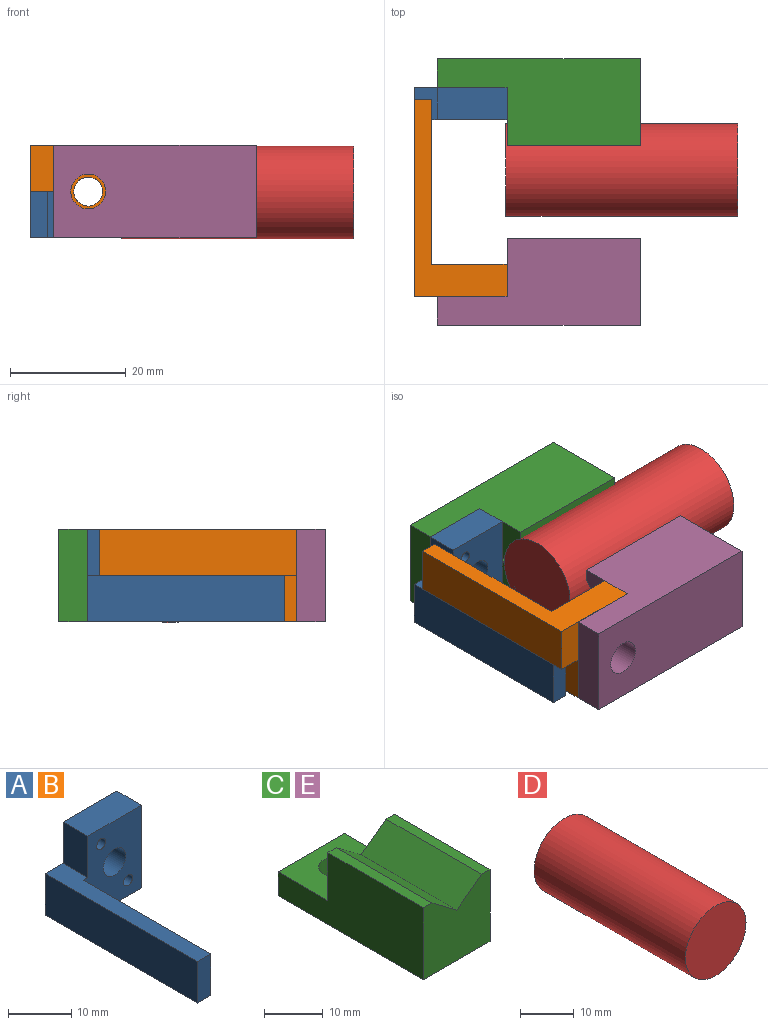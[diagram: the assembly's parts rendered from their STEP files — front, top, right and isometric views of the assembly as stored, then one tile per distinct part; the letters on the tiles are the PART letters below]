
ASSEMBLY  parts=5 mates=4
PART A: 13 faces, bbox 16x34x16 mm
  f0: plane 12x5.5mm, normal (0,0,1), area 66mm2, adj f3,f4,f5,f7
  f1: plane 34x8mm, normal (-1,0,0), area 272mm2, adj f2,f5,f6,f12
  f2: plane 34x16mm, normal (0,0,-1), area 173.5mm2, adj f1,f3,f4,f5,f11,f12
  f3: plane 16x5.5mm, normal (1,0,0), area 88mm2, adj f0,f2,f4,f5
  f4: plane 16x13mm, normal (0,-1,0), area 174.1mm2, adj f0,f2,f3,f6,f7,f8,f9,f10
  f5: plane 16x16mm, normal (0,1,0), area 198.1mm2, adj f0,f1,f2,f3,f6,f7,f8,f9
  f6: plane 34x4mm, normal (0,0,1), area 107.5mm2, adj f1,f4,f5,f7,f11,f12
  f7: plane 8x5.5mm, normal (-1,0,0), area 44mm2, adj f0,f4,f5,f6
  f8: cylinder r=1mm len=5.5mm, axis (0,-1,0), area 34.6mm2, adj f4,f5
  f9: cylinder r=2.5mm len=5.5mm, axis (0,-1,0), area 86.4mm2, adj f4,f5
  f10: cylinder r=1mm len=5.5mm, axis (0,-1,0), area 34.6mm2, adj f4,f5
  f11: plane 28.5x8mm, normal (1,0,0), area 228mm2, adj f2,f4,f6,f12
  f12: plane 8x3mm, normal (0,-1,0), area 24mm2, adj f1,f2,f6,f11
PART B: same geometry as A
PART C: 12 faces, bbox 16x35x15 mm
  f0: plane 16x12mm, normal (0,0,1), area 163.7mm2, adj f1,f2,f4,f6,f7
  f1: plane 16x5mm, normal (0,1,0), area 80mm2, adj f0,f2,f4,f5
  f2: plane 35x15mm, normal (-1,0,0), area 405mm2, adj f0,f1,f3,f5,f7,f9
  f3: plane 16x15mm, normal (0,-1,0), area 213.2mm2, adj f2,f4,f5,f8,f9,f10,f11
  f4: plane 35x15mm, normal (1,0,0), area 405mm2, adj f0,f1,f3,f5,f7,f8
  f5: plane 35x16mm, normal (0,0,-1), area 531.7mm2, adj f1,f2,f3,f4,f6
  f6: cylinder r=3mm len=6mm, axis (0,0,1), area 94.2mm2, adj f0,f5
  f7: plane 16x10mm, normal (0,1,0), area 133.2mm2, adj f0,f2,f4,f8,f9,f10,f11
  f8: plane 23x2.04mm, normal (0,0,1), area 46.9mm2, adj f3,f4,f7,f11
  f9: plane 23x2.04mm, normal (0,0,1), area 46.9mm2, adj f2,f3,f7,f10
  f10: plane 23x5.96mm, normal (0.6,0,0.8), area 171.7mm2, adj f3,f7,f9,f11
  f11: plane 23x5.96mm, normal (-0.6,0,0.8), area 171.7mm2, adj f3,f7,f8,f10
PART D: 3 faces, bbox 16x40x16 mm
  f0: cylinder r=8mm len=40mm, axis (0,1,0), area 2010.6mm2, adj f1,f2
  f1: plane 16x16mm, normal (0,-1,0), area 201.1mm2, adj f0
  f2: plane 16x16mm, normal (0,1,0), area 201.1mm2, adj f0
PART E: same geometry as C
PLACE A t=(13.02,-19.53,9.94)mm fixed
PLACE B rot(axis=(1,0,0),180deg) t=(13.02,-55.53,-6.06)mm
PLACE C rot(axis=(0.58,-0.58,0.58),120deg) t=(1.02,-14.53,9.94)mm
PLACE D rot(axis=(0.67,0.67,-0.33),143.1deg) t=(52.82,-33.75,1.79)mm
PLACE E rot(axis=(-0.58,0.58,0.58),120deg) t=(1.02,-60.53,-6.06)mm
MATE parallel D.f0 <-> B.f11  axis (-1,0,0) through (12.82,-33.75,1.79)mm
MATE fastened C.f0 <-> A.f5  axis (0,-1,0) through (13.02,-19.53,1.94)mm
MATE fastened B.f3 <-> E.f7  axis (1,0,0) through (13.02,-55.53,1.94)mm
MATE slider A.f4 <-> B.f4  axis (0,-1,0) through (0.02,-25.03,1.94)mm
